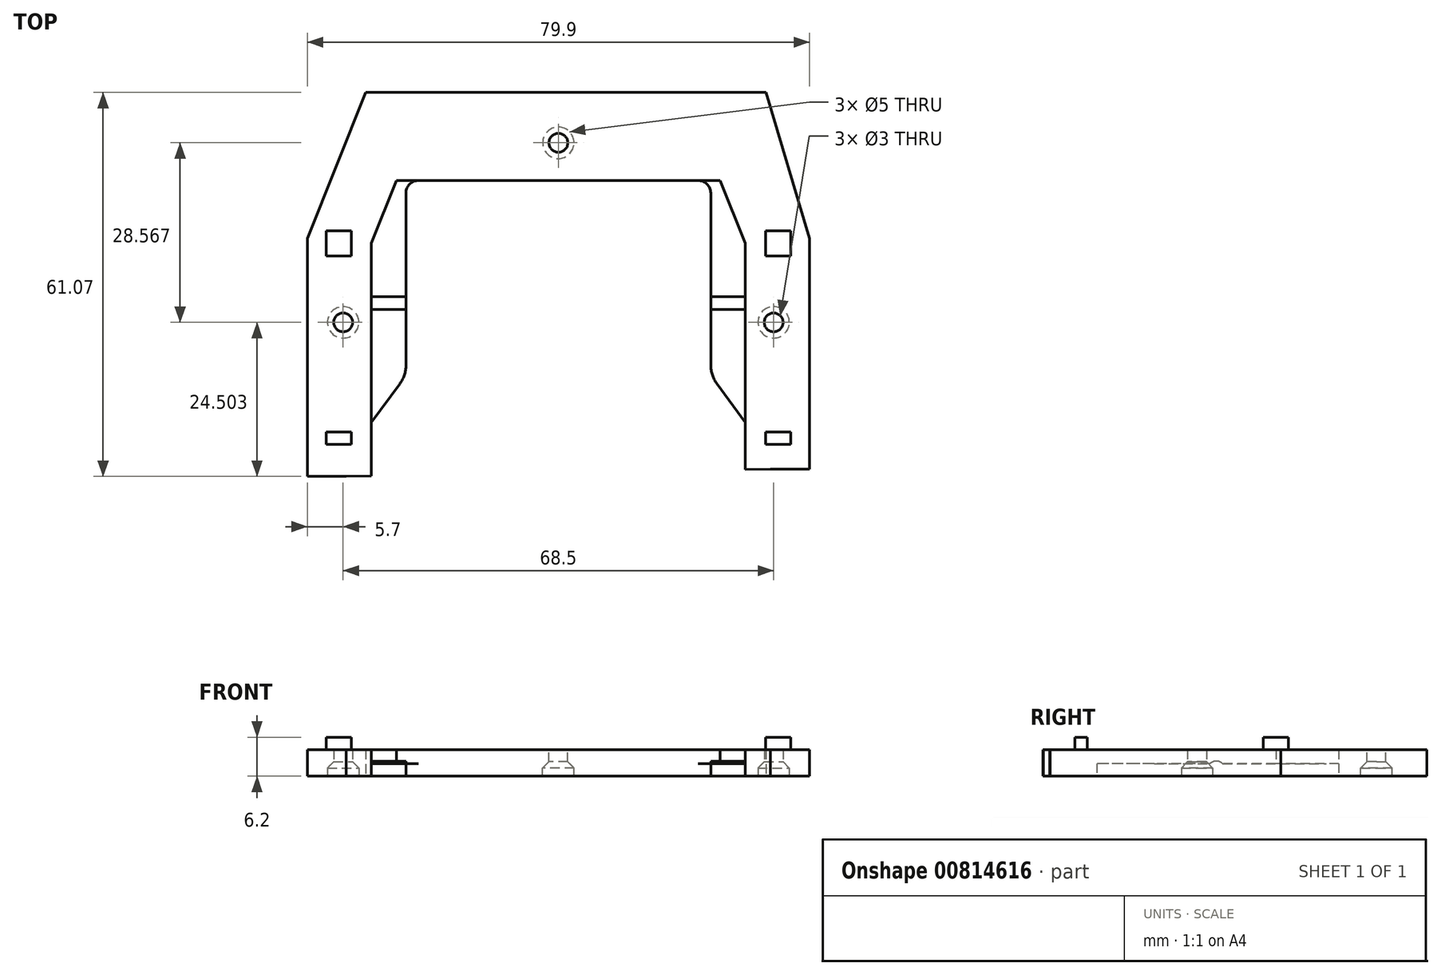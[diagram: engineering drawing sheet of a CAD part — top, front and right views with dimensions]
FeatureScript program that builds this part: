
annotation { "Feature Type Name" : "Feature", "Feature Type Description" : "" }
export const myFeature = defineFeature(function(context is Context, id is Id, definition is map)
    precondition{}
    {
        {
            var Q0;
            Q0=qCreatedBy(makeId("Top.planeOp"),FACE);
            var sketch = newSketch(context, id + "F0", { "sketchPlane" : qUnion([Q0])});
            skLineSegment(sketch, "E0.bottom", {"start": v(-25.5, 14.25) * mm, "end": v(26, 14.25) * mm});
            skLineSegment(sketch, "E0.left", {"start": v(-29.5, 4.25) * mm, "end": v(-29.5, -35.75) * mm});
            skLineSegment(sketch, "E0.right", {"start": v(30, 4.25) * mm, "end": v(30, -35.75) * mm});
            skLineSegment(sketch, "E1", {"start": v(-25.5, 14.25) * mm, "end": v(-29.5, 4.25) * mm});
            skPoint(sketch, "E2.orphan", {"position": v(-29.5, 14.25) * mm});
            skLineSegment(sketch, "E3", {"start": v(26, 14.25) * mm, "end": v(30, 4.25) * mm});
            skPoint(sketch, "E4.orphan", {"position": v(30, 14.25) * mm});
            skLineSegment(sketch, "E5.0", {"start": v(-24.2, 28.25) * mm, "end": v(-33.5, 5.02) * mm});
            skLineSegment(sketch, "E5.1", {"start": v(-33.5, -32.82) * mm, "end": v(34, -31.68) * mm});
            skLineSegment(sketch, "E5.2", {"start": v(34, 5.02) * mm, "end": v(34, -31.68) * mm});
            skLineSegment(sketch, "E5.3", {"start": v(-33.5, 5.02) * mm, "end": v(-33.5, -32.82) * mm});
            skLineSegment(sketch, "E5.4", {"start": v(27.1, 28.25) * mm, "end": v(34, 5.02) * mm});
            skLineSegment(sketch, "E5.5", {"start": v(-24.2, 28.25) * mm, "end": v(27.1, 28.25) * mm});
            skLineSegment(sketch, "E6", {"start": v(-29.5, -32.75) * mm, "end": v(-29.5, -35.75) * mm});
            skLineSegment(sketch, "E7", {"start": v(30, -32.75) * mm, "end": v(30, -35.75) * mm});
            skLineSegment(sketch, "E8.bottom", {"start": v(-29.5, -32.75) * mm, "end": v(30, -31.75) * mm});
            skLineSegment(sketch, "E8.left", {"start": v(-29.5, -32.75) * mm, "end": v(-29.5, -24.25) * mm});
            skLineSegment(sketch, "E8.right", {"start": v(30, -31.75) * mm, "end": v(30, -24.25) * mm});
            skLineSegment(sketch, "E9.top", {"start": v(-22, 14.25) * mm, "end": v(22.5, 14.25) * mm});
            skLineSegment(sketch, "E9.left", {"start": v(-24, -16.75) * mm, "end": v(-24, 12.25) * mm});
            skLineSegment(sketch, "E9.right", {"start": v(24.5, -16.75) * mm, "end": v(24.5, 12.25) * mm});
            skPoint(sketch, "E10.visualSharp", {"position": v(-24, 14.25) * mm});
            skArc(sketch, "E10.filletArc", {"start": v(-22, 14.25) * mm, "mid": v(-23.41, 13.66) * mm, "end": v(-24, 12.25) * mm});
            skPoint(sketch, "E11.visualSharp", {"position": v(24.5, 14.25) * mm});
            skArc(sketch, "E11.filletArc", {"start": v(24.5, 12.25) * mm, "mid": v(23.91, 13.66) * mm, "end": v(22.5, 14.25) * mm});
            skLineSegment(sketch, "E12", {"start": v(24.5, -16.75) * mm, "end": v(30, -24.25) * mm});
            skLineSegment(sketch, "E13", {"start": v(-24, -16.75) * mm, "end": v(-29.5, -24.25) * mm});
            skPoint(sketch, "E14.orphan", {"position": v(-29.5, -15.75) * mm});
            skPoint(sketch, "E15.orphan", {"position": v(30, -16.75) * mm});
            skSolve(sketch);
        }
        {
            var Q0;
            {var subQ0=sQuery(id+"F0.wireOp",EDGE,"E1");var subQ5=sQuery(id+"F0.wireOp",EDGE,"E3");Q0=qUnion([makeQuery(id+"F0.imprint","IMPRINT",FACE,{"disambiguationData":[TD([[makeQuery(id+"F0.imprint","IMPRINT",EDGE,{"derivedFrom":subQ5}),-1.0]])]}),makeQuery(id+"F0.imprint","IMPRINT",FACE,{"disambiguationData":[TD([[makeQuery(id+"F0.imprint","IMPRINT",EDGE,{"derivedFrom":subQ0}),1.0]])]})]);}
            extrude(context, id + "F1", {"entities" : qUnion([Q0]), "depth" : 2 * mm, "offsetDistance" : 25 * mm});
        }
        {
            var Q0;
            {var subQ1=sQuery(id+"F0.wireOp",EDGE,"E1");Q0=makeQuery(id+"F0.imprint","IMPRINT",FACE,{"disambiguationData":[TD([[makeQuery(id+"F0.imprint","IMPRINT",EDGE,{"derivedFrom":subQ1}),-1.0]])]});}
            extrude(context, id + "F2", {"entities" : qUnion([Q0]), "operationType" : NewBodyOperationType.ADD, "depth" : 4.2 * mm, "offsetDistance" : 25 * mm});
        }
        {
            var Q0;
            Q0=makeQuery(id+"F2.opExtrude","SWEPT_FACE",FACE,{"disambiguationData":[OSD([sQuery(id+"F0.wireOp",EDGE,"E5.3")])]});
            var Q1;
            Q1=makeQuery(id+"F2.opExtrude","SWEPT_FACE",FACE,{"disambiguationData":[OSD([sQuery(id+"F0.wireOp",EDGE,"E5.0")])]});
            extrude(context, id + "F3", {"entities" : qUnion([Q0, Q1]), "operationType" : NewBodyOperationType.ADD, "depth" : 6.2 * mm, "offsetDistance" : 25 * mm});
        }
        {
            var Q0;
            Q0=makeQuery(id+"F2.opExtrude","SWEPT_FACE",FACE,{"disambiguationData":[OSD([sQuery(id+"F0.wireOp",EDGE,"E5.2")])]});
            var Q1;
            Q1=makeQuery(id+"F2.opExtrude","SWEPT_FACE",FACE,{"disambiguationData":[OSD([sQuery(id+"F0.wireOp",EDGE,"E5.4")])]});
            extrude(context, id + "F4", {"entities" : qUnion([Q0, Q1]), "operationType" : NewBodyOperationType.ADD, "depth" : 6.2 * mm, "offsetDistance" : 25 * mm});
        }
        {
            var Q0;
            {var subQ0=sQuery(id+"F0.wireOp",EDGE,"E5.4");var subQ1=sQuery(id+"F0.wireOp",EDGE,"E5.2");var subQ2=sQuery(id+"F0.wireOp",EDGE,"E5.3");var subQ3=sQuery(id+"F0.wireOp",EDGE,"E5.0");Q0=makeQuery(id+"F4.boolean.opBoolean","MERGE",FACE,{"derivedFrom":[makeQuery(id+"F3.boolean.opBoolean","MERGE",FACE,{"derivedFrom":[makeQuery(id+"F2.opExtrude","CAP_FACE",FACE,{"disambiguationData":[OSD([sQuery(id+"F0.wireOp",EDGE,"E0.bottom"),sQuery(id+"F0.wireOp",EDGE,"E0.left"),sQuery(id+"F0.wireOp",EDGE,"E0.right"),sQuery(id+"F0.wireOp",EDGE,"E1"),sQuery(id+"F0.wireOp",EDGE,"E3"),subQ3,sQuery(id+"F0.wireOp",EDGE,"E5.1"),subQ1,subQ2,subQ0,sQuery(id+"F0.wireOp",EDGE,"E5.5")])],"isStart":false}),makeQuery(id+"F3.opExtrude","SWEPT_FACE",FACE,{"disambiguationData":[OSD([subQ3]),TDD([makeQuery(id+"F2.opExtrude","CAP_EDGE",EDGE,{"disambiguationData":[OSD([subQ3])],"isStart":false})])]}),makeQuery(id+"F3.opExtrude","SWEPT_FACE",FACE,{"disambiguationData":[OSD([subQ2]),TDD([makeQuery(id+"F2.opExtrude","CAP_EDGE",EDGE,{"disambiguationData":[OSD([subQ2])],"isStart":false})])]})]}),makeQuery(id+"F4.opExtrude","SWEPT_FACE",FACE,{"disambiguationData":[OSD([subQ1]),TDD([makeQuery(id+"F2.opExtrude","CAP_EDGE",EDGE,{"disambiguationData":[OSD([subQ1])],"isStart":false})])]}),makeQuery(id+"F4.opExtrude","SWEPT_FACE",FACE,{"disambiguationData":[OSD([subQ0]),TDD([makeQuery(id+"F2.opExtrude","CAP_EDGE",EDGE,{"disambiguationData":[OSD([subQ0])],"isStart":false})])]})]});}
            var sketch = newSketch(context, id + "F5", { "sketchPlane" : qUnion([Q0])});
            skLineSegment(sketch, "E16.bottom", {"start": v(-36.7, -27.75) * mm, "end": v(-32.7, -27.75) * mm});
            skLineSegment(sketch, "E16.top", {"start": v(-36.7, -25.75) * mm, "end": v(-32.7, -25.75) * mm});
            skLineSegment(sketch, "E16.left", {"start": v(-36.7, -27.75) * mm, "end": v(-36.7, -25.75) * mm});
            skLineSegment(sketch, "E16.right", {"start": v(-32.7, -27.75) * mm, "end": v(-32.7, -25.75) * mm});
            skLineSegment(sketch, "E17.bottom", {"start": v(37.2, -27.75) * mm, "end": v(33.2, -27.75) * mm});
            skLineSegment(sketch, "E17.top", {"start": v(37.2, -25.75) * mm, "end": v(33.2, -25.75) * mm});
            skLineSegment(sketch, "E17.left", {"start": v(37.2, -27.75) * mm, "end": v(37.2, -25.75) * mm});
            skLineSegment(sketch, "E17.right", {"start": v(33.2, -27.75) * mm, "end": v(33.2, -25.75) * mm});
            skLineSegment(sketch, "E18.bottom", {"start": v(33.2, 2.25) * mm, "end": v(37.2, 2.25) * mm});
            skLineSegment(sketch, "E18.top", {"start": v(33.2, 6.25) * mm, "end": v(37.2, 6.25) * mm});
            skLineSegment(sketch, "E18.left", {"start": v(33.2, 2.25) * mm, "end": v(33.2, 6.25) * mm});
            skLineSegment(sketch, "E18.right", {"start": v(37.2, 2.25) * mm, "end": v(37.2, 6.25) * mm});
            skLineSegment(sketch, "E19.bottom", {"start": v(-36.7, 2.25) * mm, "end": v(-32.7, 2.25) * mm});
            skLineSegment(sketch, "E19.top", {"start": v(-36.7, 6.25) * mm, "end": v(-32.7, 6.25) * mm});
            skLineSegment(sketch, "E19.left", {"start": v(-36.7, 2.25) * mm, "end": v(-36.7, 6.25) * mm});
            skLineSegment(sketch, "E19.right", {"start": v(-32.7, 2.25) * mm, "end": v(-32.7, 6.25) * mm});
            skSolve(sketch);
        }
        {
            var Q0;
            Q0=qSketchRegion(id+"F5",true);
            extrude(context, id + "F6", {"entities" : qUnion([Q0]), "operationType" : NewBodyOperationType.ADD, "depth" : 2 * mm, "offsetDistance" : 25 * mm});
        }
        {
            var Q0;
            {var subQ0=sQuery(id+"F0.wireOp",EDGE,"E5.4");var subQ1=sQuery(id+"F0.wireOp",EDGE,"E5.2");var subQ2=sQuery(id+"F0.wireOp",EDGE,"E5.3");var subQ3=sQuery(id+"F0.wireOp",EDGE,"E5.0");var subQ4=sQuery(id+"F0.wireOp",EDGE,"E3");var subQ5=sQuery(id+"F0.wireOp",EDGE,"E1");var subQ6=sQuery(id+"F0.wireOp",EDGE,"E0.right");var subQ7=sQuery(id+"F0.wireOp",EDGE,"E0.left");var subQ8=sQuery(id+"F0.wireOp",EDGE,"E0.bottom");Q0=makeQuery(id+"F4.boolean.opBoolean","MERGE",FACE,{"derivedFrom":[makeQuery(id+"F3.boolean.opBoolean","MERGE",FACE,{"derivedFrom":[makeQuery(id+"F2.boolean.opBoolean","MERGE",FACE,{"derivedFrom":[makeQuery(id+"F1.opExtrude","CAP_FACE",FACE,{"disambiguationData":[OSD([subQ8,subQ6,subQ4,sQuery(id+"F0.wireOp",EDGE,"E9.right"),sQuery(id+"F0.wireOp",EDGE,"E11.filletArc"),sQuery(id+"F0.wireOp",EDGE,"E12")])],"isStart":true}),makeQuery(id+"F1.opExtrude","CAP_FACE",FACE,{"disambiguationData":[OSD([subQ8,subQ7,subQ5,sQuery(id+"F0.wireOp",EDGE,"E9.left"),sQuery(id+"F0.wireOp",EDGE,"E10.filletArc"),sQuery(id+"F0.wireOp",EDGE,"E13")])],"isStart":true}),makeQuery(id+"F2.opExtrude","CAP_FACE",FACE,{"disambiguationData":[OSD([subQ8,subQ7,subQ6,subQ5,subQ4,subQ3,sQuery(id+"F0.wireOp",EDGE,"E5.1"),subQ1,subQ2,subQ0,sQuery(id+"F0.wireOp",EDGE,"E5.5")])],"isStart":true})]}),makeQuery(id+"F3.opExtrude","SWEPT_FACE",FACE,{"disambiguationData":[OSD([subQ3]),TDD([makeQuery(id+"F2.opExtrude","CAP_EDGE",EDGE,{"disambiguationData":[OSD([subQ3])],"isStart":true})])]}),makeQuery(id+"F3.opExtrude","SWEPT_FACE",FACE,{"disambiguationData":[OSD([subQ2]),TDD([makeQuery(id+"F2.opExtrude","CAP_EDGE",EDGE,{"disambiguationData":[OSD([subQ2])],"isStart":true})])]})]}),makeQuery(id+"F4.opExtrude","SWEPT_FACE",FACE,{"disambiguationData":[OSD([subQ1]),TDD([makeQuery(id+"F2.opExtrude","CAP_EDGE",EDGE,{"disambiguationData":[OSD([subQ1])],"isStart":true})])]}),makeQuery(id+"F4.opExtrude","SWEPT_FACE",FACE,{"disambiguationData":[OSD([subQ0]),TDD([makeQuery(id+"F2.opExtrude","CAP_EDGE",EDGE,{"disambiguationData":[OSD([subQ0])],"isStart":true})])]})]});}
            var sketch = newSketch(context, id + "F7", { "sketchPlane" : qUnion([Q0])});
            skCircle(sketch, "E20", {"center": v(-34, 8.32) * mm, "radius": 2.5 * mm});
            skCircle(sketch, "E21", {"center": v(34.5, 8.32) * mm, "radius": 2.5 * mm});
            skCircle(sketch, "E22", {"center": v(-34, 8.32) * mm, "radius": 1.5 * mm});
            skCircle(sketch, "E23", {"center": v(34.5, 8.32) * mm, "radius": 1.5 * mm});
            skSolve(sketch);
        }
        {
            var Q0;
            Q0=qSketchRegion(id+"F7",true);
            extrude(context, id + "F8", {"entities" : qUnion([Q0]), "operationType" : NewBodyOperationType.REMOVE, "oppositeDirection" : true, "depth" : 2.5 * mm, "offsetDistance" : 25 * mm});
        }
        {
            var Q0;
            {var subQ0=sQuery(id+"F0.wireOp",EDGE,"E5.4");var subQ1=sQuery(id+"F0.wireOp",EDGE,"E5.2");var subQ2=sQuery(id+"F0.wireOp",EDGE,"E5.3");var subQ3=sQuery(id+"F0.wireOp",EDGE,"E5.0");var subQ4=sQuery(id+"F0.wireOp",EDGE,"E3");var subQ5=sQuery(id+"F0.wireOp",EDGE,"E1");var subQ6=sQuery(id+"F0.wireOp",EDGE,"E0.right");var subQ7=sQuery(id+"F0.wireOp",EDGE,"E0.left");var subQ8=sQuery(id+"F0.wireOp",EDGE,"E0.bottom");Q0=makeQuery(id+"F8.boolean.opBoolean","SPLIT",FACE,{"disambiguationData":[TD([makeQuery(id+"F8.opExtrude","SWEPT_FACE",FACE,{"disambiguationData":[OSD([sQuery(id+"F7.wireOp",EDGE,"E22")])]})])],"derivedFrom":makeQuery(id+"F4.boolean.opBoolean","MERGE",FACE,{"derivedFrom":[makeQuery(id+"F3.boolean.opBoolean","MERGE",FACE,{"derivedFrom":[makeQuery(id+"F2.boolean.opBoolean","MERGE",FACE,{"derivedFrom":[makeQuery(id+"F1.opExtrude","CAP_FACE",FACE,{"disambiguationData":[OSD([subQ8,subQ6,subQ4,sQuery(id+"F0.wireOp",EDGE,"E9.right"),sQuery(id+"F0.wireOp",EDGE,"E11.filletArc"),sQuery(id+"F0.wireOp",EDGE,"E12")])],"isStart":true}),makeQuery(id+"F1.opExtrude","CAP_FACE",FACE,{"disambiguationData":[OSD([subQ8,subQ7,subQ5,sQuery(id+"F0.wireOp",EDGE,"E9.left"),sQuery(id+"F0.wireOp",EDGE,"E10.filletArc"),sQuery(id+"F0.wireOp",EDGE,"E13")])],"isStart":true}),makeQuery(id+"F2.opExtrude","CAP_FACE",FACE,{"disambiguationData":[OSD([subQ8,subQ7,subQ6,subQ5,subQ4,subQ3,sQuery(id+"F0.wireOp",EDGE,"E5.1"),subQ1,subQ2,subQ0,sQuery(id+"F0.wireOp",EDGE,"E5.5")])],"isStart":true})]}),makeQuery(id+"F3.opExtrude","SWEPT_FACE",FACE,{"disambiguationData":[OSD([subQ3]),TDD([makeQuery(id+"F2.opExtrude","CAP_EDGE",EDGE,{"disambiguationData":[OSD([subQ3])],"isStart":true})])]}),makeQuery(id+"F3.opExtrude","SWEPT_FACE",FACE,{"disambiguationData":[OSD([subQ2]),TDD([makeQuery(id+"F2.opExtrude","CAP_EDGE",EDGE,{"disambiguationData":[OSD([subQ2])],"isStart":true})])]})]}),makeQuery(id+"F4.opExtrude","SWEPT_FACE",FACE,{"disambiguationData":[OSD([subQ1]),TDD([makeQuery(id+"F2.opExtrude","CAP_EDGE",EDGE,{"disambiguationData":[OSD([subQ1])],"isStart":true})])]}),makeQuery(id+"F4.opExtrude","SWEPT_FACE",FACE,{"disambiguationData":[OSD([subQ0]),TDD([makeQuery(id+"F2.opExtrude","CAP_EDGE",EDGE,{"disambiguationData":[OSD([subQ0])],"isStart":true})])]})]})});}
            var Q1;
            {var subQ0=sQuery(id+"F0.wireOp",EDGE,"E5.4");var subQ1=sQuery(id+"F0.wireOp",EDGE,"E5.2");var subQ2=sQuery(id+"F0.wireOp",EDGE,"E5.3");var subQ3=sQuery(id+"F0.wireOp",EDGE,"E5.0");var subQ4=sQuery(id+"F0.wireOp",EDGE,"E3");var subQ5=sQuery(id+"F0.wireOp",EDGE,"E1");var subQ6=sQuery(id+"F0.wireOp",EDGE,"E0.right");var subQ7=sQuery(id+"F0.wireOp",EDGE,"E0.left");var subQ8=sQuery(id+"F0.wireOp",EDGE,"E0.bottom");Q1=makeQuery(id+"F8.boolean.opBoolean","SPLIT",FACE,{"disambiguationData":[TD([makeQuery(id+"F8.opExtrude","SWEPT_FACE",FACE,{"disambiguationData":[OSD([sQuery(id+"F7.wireOp",EDGE,"E23")])]})])],"derivedFrom":makeQuery(id+"F4.boolean.opBoolean","MERGE",FACE,{"derivedFrom":[makeQuery(id+"F3.boolean.opBoolean","MERGE",FACE,{"derivedFrom":[makeQuery(id+"F2.boolean.opBoolean","MERGE",FACE,{"derivedFrom":[makeQuery(id+"F1.opExtrude","CAP_FACE",FACE,{"disambiguationData":[OSD([subQ8,subQ6,subQ4,sQuery(id+"F0.wireOp",EDGE,"E9.right"),sQuery(id+"F0.wireOp",EDGE,"E11.filletArc"),sQuery(id+"F0.wireOp",EDGE,"E12")])],"isStart":true}),makeQuery(id+"F1.opExtrude","CAP_FACE",FACE,{"disambiguationData":[OSD([subQ8,subQ7,subQ5,sQuery(id+"F0.wireOp",EDGE,"E9.left"),sQuery(id+"F0.wireOp",EDGE,"E10.filletArc"),sQuery(id+"F0.wireOp",EDGE,"E13")])],"isStart":true}),makeQuery(id+"F2.opExtrude","CAP_FACE",FACE,{"disambiguationData":[OSD([subQ8,subQ7,subQ6,subQ5,subQ4,subQ3,sQuery(id+"F0.wireOp",EDGE,"E5.1"),subQ1,subQ2,subQ0,sQuery(id+"F0.wireOp",EDGE,"E5.5")])],"isStart":true})]}),makeQuery(id+"F3.opExtrude","SWEPT_FACE",FACE,{"disambiguationData":[OSD([subQ3]),TDD([makeQuery(id+"F2.opExtrude","CAP_EDGE",EDGE,{"disambiguationData":[OSD([subQ3])],"isStart":true})])]}),makeQuery(id+"F3.opExtrude","SWEPT_FACE",FACE,{"disambiguationData":[OSD([subQ2]),TDD([makeQuery(id+"F2.opExtrude","CAP_EDGE",EDGE,{"disambiguationData":[OSD([subQ2])],"isStart":true})])]})]}),makeQuery(id+"F4.opExtrude","SWEPT_FACE",FACE,{"disambiguationData":[OSD([subQ1]),TDD([makeQuery(id+"F2.opExtrude","CAP_EDGE",EDGE,{"disambiguationData":[OSD([subQ1])],"isStart":true})])]}),makeQuery(id+"F4.opExtrude","SWEPT_FACE",FACE,{"disambiguationData":[OSD([subQ0]),TDD([makeQuery(id+"F2.opExtrude","CAP_EDGE",EDGE,{"disambiguationData":[OSD([subQ0])],"isStart":true})])]})]})});}
            extrude(context, id + "F9", {"entities" : qUnion([Q0, Q1]), "operationType" : NewBodyOperationType.REMOVE, "oppositeDirection" : true, "depth" : 4.5 * mm, "offsetDistance" : 25 * mm});
        }
        {
            var Q0;
            Q0=makeQuery(id+"F1.opExtrude","SWEPT_EDGE",EDGE,{"disambiguationData":[OSD([sQuery(id+"F0.wireOp",EDGE,"E9.right"),sQuery(id+"F0.wireOp",EDGE,"E12")])]});
            var Q1;
            Q1=makeQuery(id+"F1.opExtrude","SWEPT_EDGE",EDGE,{"disambiguationData":[OSD([sQuery(id+"F0.wireOp",EDGE,"E9.left"),sQuery(id+"F0.wireOp",EDGE,"E13")])]});
            fillet(context, id + "F10", {"entities" : qUnion([Q0, Q1]), "radius" : 5 * mm, "tangentPropagation" : true, "allowEdgeOverflow" : false});
        }
        {
            var Q0;
            {var subQ0=sQuery(id+"F0.wireOp",EDGE,"E5.4");var subQ1=sQuery(id+"F0.wireOp",EDGE,"E5.2");var subQ2=sQuery(id+"F0.wireOp",EDGE,"E5.3");var subQ3=sQuery(id+"F0.wireOp",EDGE,"E5.0");Q0=makeQuery(id+"F4.boolean.opBoolean","MERGE",FACE,{"derivedFrom":[makeQuery(id+"F3.boolean.opBoolean","MERGE",FACE,{"derivedFrom":[makeQuery(id+"F2.opExtrude","CAP_FACE",FACE,{"disambiguationData":[OSD([sQuery(id+"F0.wireOp",EDGE,"E0.bottom"),sQuery(id+"F0.wireOp",EDGE,"E0.left"),sQuery(id+"F0.wireOp",EDGE,"E0.right"),sQuery(id+"F0.wireOp",EDGE,"E1"),sQuery(id+"F0.wireOp",EDGE,"E3"),subQ3,sQuery(id+"F0.wireOp",EDGE,"E5.1"),subQ1,subQ2,subQ0,sQuery(id+"F0.wireOp",EDGE,"E5.5")])],"isStart":false}),makeQuery(id+"F3.opExtrude","SWEPT_FACE",FACE,{"disambiguationData":[OSD([subQ3]),TDD([makeQuery(id+"F2.opExtrude","CAP_EDGE",EDGE,{"disambiguationData":[OSD([subQ3])],"isStart":false})])]}),makeQuery(id+"F3.opExtrude","SWEPT_FACE",FACE,{"disambiguationData":[OSD([subQ2]),TDD([makeQuery(id+"F2.opExtrude","CAP_EDGE",EDGE,{"disambiguationData":[OSD([subQ2])],"isStart":false})])]})]}),makeQuery(id+"F4.opExtrude","SWEPT_FACE",FACE,{"disambiguationData":[OSD([subQ1]),TDD([makeQuery(id+"F2.opExtrude","CAP_EDGE",EDGE,{"disambiguationData":[OSD([subQ1])],"isStart":false})])]}),makeQuery(id+"F4.opExtrude","SWEPT_FACE",FACE,{"disambiguationData":[OSD([subQ0]),TDD([makeQuery(id+"F2.opExtrude","CAP_EDGE",EDGE,{"disambiguationData":[OSD([subQ0])],"isStart":false})])]})]});}
            var sketch = newSketch(context, id + "F11", { "sketchPlane" : qUnion([Q0])});
            skCircle(sketch, "E24", {"center": v(0.25, 20.25) * mm, "radius": 1.5 * mm});
            skCircle(sketch, "E25", {"center": v(0.25, 20.25) * mm, "radius": 2.5 * mm});
            skSolve(sketch);
        }
        {
            var Q0;
            Q0=qSketchRegion(id+"F11",true);
            extrude(context, id + "F12", {"entities" : qUnion([Q0]), "operationType" : NewBodyOperationType.REMOVE, "oppositeDirection" : true, "depth" : 6.8 * mm, "offsetDistance" : 25 * mm, "hasSecondDirection" : true, "secondDirectionOppositeDirection" : true, "secondDirectionDepth" : 1.7 * mm});
        }
        {
            var Q0;
            Q0=makeQuery(id+"F11.imprint","IMPRINT",FACE,{"disambiguationData":[TD([[makeQuery(id+"F11.imprint","IMPRINT",EDGE,{"derivedFrom":sQuery(id+"F11.wireOp",EDGE,"E24")}),1.0]])]});
            extrude(context, id + "F13", {"entities" : qUnion([Q0]), "operationType" : NewBodyOperationType.REMOVE, "oppositeDirection" : true, "depth" : 4.2 * mm, "offsetDistance" : 25 * mm});
        }
        {
            var Q0;
            Q0=makeQuery(id+"F1.opExtrude","CAP_FACE",FACE,{"disambiguationData":[OSD([sQuery(id+"F0.wireOp",EDGE,"E0.bottom"),sQuery(id+"F0.wireOp",EDGE,"E0.right"),sQuery(id+"F0.wireOp",EDGE,"E3"),sQuery(id+"F0.wireOp",EDGE,"E9.right"),sQuery(id+"F0.wireOp",EDGE,"E11.filletArc"),sQuery(id+"F0.wireOp",EDGE,"E12")])],"isStart":false});
            var sketch = newSketch(context, id + "F14", { "sketchPlane" : qUnion([Q0])});
            skLineSegment(sketch, "E26.bottom", {"start": v(30, -6.25) * mm, "end": v(24.5, -6.25) * mm});
            skLineSegment(sketch, "E26.top", {"start": v(30, -4.25) * mm, "end": v(24.5, -4.25) * mm});
            skLineSegment(sketch, "E26.left", {"start": v(30, -6.25) * mm, "end": v(30, -4.25) * mm});
            skLineSegment(sketch, "E26.right", {"start": v(24.5, -6.25) * mm, "end": v(24.5, -4.25) * mm});
            skLineSegment(sketch, "E27.bottom", {"start": v(-29.5, -4.25) * mm, "end": v(-24, -4.25) * mm});
            skLineSegment(sketch, "E27.top", {"start": v(-29.5, -6.25) * mm, "end": v(-24, -6.25) * mm});
            skLineSegment(sketch, "E27.left", {"start": v(-29.5, -4.25) * mm, "end": v(-29.5, -6.25) * mm});
            skLineSegment(sketch, "E27.right", {"start": v(-24, -4.25) * mm, "end": v(-24, -6.25) * mm});
            skSolve(sketch);
        }
        {
            var Q0;
            Q0=qSketchRegion(id+"F14",true);
            extrude(context, id + "F15", {"entities" : qUnion([Q0]), "operationType" : NewBodyOperationType.ADD, "depth" : 0.4 * mm, "offsetDistance" : 25 * mm});
        }
        {
            var Q0;
            Q0=makeQuery(id+"F15.opExtrude","CAP_EDGE",EDGE,{"disambiguationData":[OSD([sQuery(id+"F14.wireOp",EDGE,"E27.top")])],"isStart":false});
            var Q1;
            Q1=makeQuery(id+"F15.opExtrude","CAP_EDGE",EDGE,{"disambiguationData":[OSD([sQuery(id+"F14.wireOp",EDGE,"E27.bottom")])],"isStart":false});
            var Q2;
            Q2=makeQuery(id+"F15.opExtrude","CAP_EDGE",EDGE,{"disambiguationData":[OSD([sQuery(id+"F14.wireOp",EDGE,"E26.top")])],"isStart":false});
            var Q3;
            Q3=makeQuery(id+"F15.opExtrude","CAP_EDGE",EDGE,{"disambiguationData":[OSD([sQuery(id+"F14.wireOp",EDGE,"E26.bottom")])],"isStart":false});
            fillet(context, id + "F16", {"entities" : qUnion([Q0, Q1, Q2, Q3]), "radius" : 1.4 * mm, "tangentPropagation" : true, "allowEdgeOverflow" : false});
        }
        {
            var Q0;
            Q0=makeQuery(id+"F8.boolean.opBoolean","COPY",EDGE,{"derivedFrom":makeQuery(id+"F8.opExtrude","CAP_EDGE",EDGE,{"disambiguationData":[OSD([sQuery(id+"F7.wireOp",EDGE,"E20")])],"isStart":false})});
            var Q1;
            Q1=makeQuery(id+"F8.boolean.opBoolean","COPY",EDGE,{"derivedFrom":makeQuery(id+"F8.opExtrude","CAP_EDGE",EDGE,{"disambiguationData":[OSD([sQuery(id+"F7.wireOp",EDGE,"E21")])],"isStart":false})});
            var Q2;
            Q2=makeQuery(id+"F12.boolean.opBoolean","COPY",EDGE,{"derivedFrom":makeQuery(id+"F12.opExtrude","CAP_EDGE",EDGE,{"disambiguationData":[OSD([sQuery(id+"F11.wireOp",EDGE,"E25")])],"isStart":true})});
            chamfer(context, id + "F17", {"entities" : qUnion([Q0, Q1, Q2]), "width" : 1.2 * mm, "tangentPropagation" : true});
        }
    });
